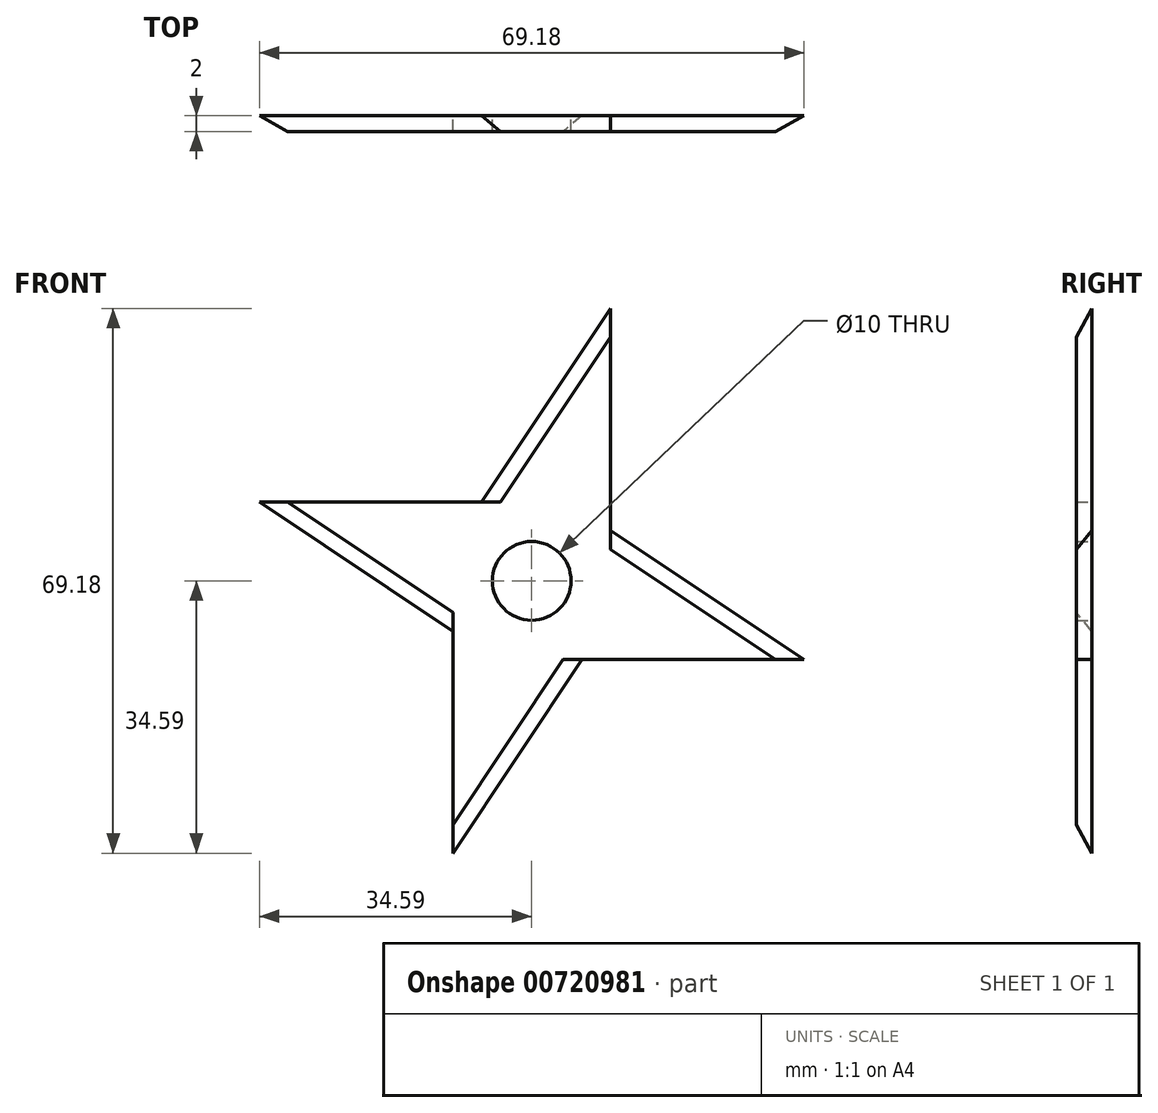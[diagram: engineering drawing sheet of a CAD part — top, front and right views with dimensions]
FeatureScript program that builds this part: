
annotation { "Feature Type Name" : "Feature", "Feature Type Description" : "" }
export const myFeature = defineFeature(function(context is Context, id is Id, definition is map)
    precondition{}
    {
        {
            var Q0;
            Q0=qCreatedBy(makeId("Front.planeOp"),FACE);
            var sketch = newSketch(context, id + "F0", { "sketchPlane" : qUnion([Q0])});
            skLineSegment(sketch, "E0.bottom", {"start": v(40, 10) * mm, "end": v(-40, 10) * mm, "construction": true});
            skLineSegment(sketch, "E0.top", {"start": v(40, -10) * mm, "end": v(-40, -10) * mm, "construction": true});
            skLineSegment(sketch, "E0.left", {"start": v(40, 10) * mm, "end": v(40, -10) * mm, "construction": true});
            skLineSegment(sketch, "E0.right", {"start": v(-40, 10) * mm, "end": v(-40, -10) * mm, "construction": true});
            skPoint(sketch, "E0.middle", {"position": v(0, 0) * mm});
            skLineSegment(sketch, "E1.bottom", {"start": v(10, 40) * mm, "end": v(-10, 40) * mm, "construction": true});
            skLineSegment(sketch, "E1.top", {"start": v(10, -40) * mm, "end": v(-10, -40) * mm, "construction": true});
            skLineSegment(sketch, "E1.left", {"start": v(10, 40) * mm, "end": v(10, -40) * mm, "construction": true});
            skLineSegment(sketch, "E1.right", {"start": v(-10, 40) * mm, "end": v(-10, -40) * mm, "construction": true});
            skPoint(sketch, "E2", {"position": v(-10, 10) * mm});
            skPoint(sketch, "E3", {"position": v(10, 10) * mm});
            skPoint(sketch, "E4", {"position": v(10, -10) * mm});
            skPoint(sketch, "E5", {"position": v(-10, -10) * mm});
            skLineSegment(sketch, "E6", {"start": v(-10, 10) * mm, "end": v(10, 40) * mm});
            skLineSegment(sketch, "E7", {"start": v(10, 10) * mm, "end": v(40, -10) * mm});
            skLineSegment(sketch, "E8", {"start": v(10, -10) * mm, "end": v(-10, -40) * mm});
            skLineSegment(sketch, "E9", {"start": v(-10, -10) * mm, "end": v(-40, 10) * mm});
            skLineSegment(sketch, "E10", {"start": v(-10, 10) * mm, "end": v(-40, 10) * mm});
            skLineSegment(sketch, "E11", {"start": v(10, 40) * mm, "end": v(10, 10) * mm});
            skLineSegment(sketch, "E12", {"start": v(10, -10) * mm, "end": v(40, -10) * mm});
            skLineSegment(sketch, "E13", {"start": v(-10, -40) * mm, "end": v(-10, -10) * mm});
            skCircle(sketch, "E14", {"center": v(0, 0) * mm, "radius": 5 * mm});
            skSolve(sketch);
        }
        {
            var Q0;
            Q0=makeQuery(id+"F0.imprint","IMPRINT",FACE,{"disambiguationData":[TD([[makeQuery(id+"F0.imprint","IMPRINT",EDGE,{"derivedFrom":sQuery(id+"F0.wireOp",EDGE,"E6")}),-1.0]])]});
            extrude(context, id + "F1", {"entities" : qUnion([Q0]), "depth" : 2 * mm, "offsetDistance" : 25 * mm});
        }
        {
            var Q0;
            Q0=makeQuery(id+"F1.opExtrude","CAP_EDGE",EDGE,{"disambiguationData":[OSD([sQuery(id+"F0.wireOp",EDGE,"E7")])],"isStart":false});
            var Q1;
            Q1=makeQuery(id+"F1.opExtrude","CAP_EDGE",EDGE,{"disambiguationData":[OSD([sQuery(id+"F0.wireOp",EDGE,"E6")])],"isStart":false});
            var Q2;
            Q2=makeQuery(id+"F1.opExtrude","CAP_EDGE",EDGE,{"disambiguationData":[OSD([sQuery(id+"F0.wireOp",EDGE,"E9")])],"isStart":false});
            var Q3;
            Q3=makeQuery(id+"F1.opExtrude","CAP_EDGE",EDGE,{"disambiguationData":[OSD([sQuery(id+"F0.wireOp",EDGE,"E8")])],"isStart":false});
            chamfer(context, id + "F2", {"entities" : qUnion([Q0, Q1, Q2, Q3]), "width" : 5 * mm, "tangentPropagation" : true});
        }
    });
